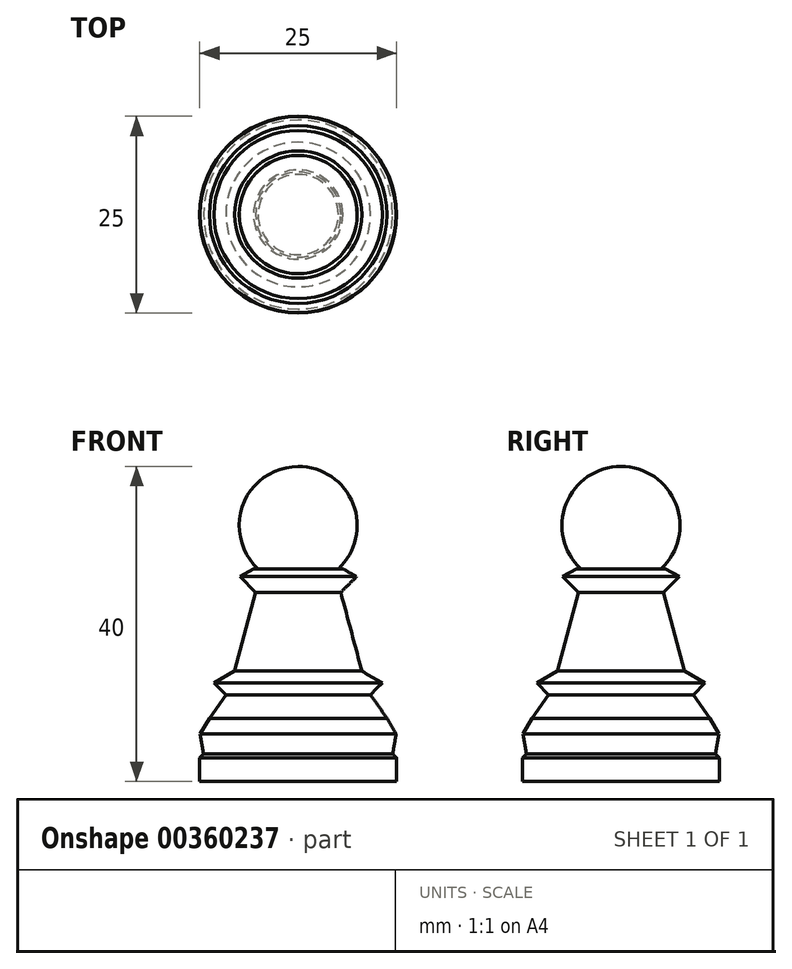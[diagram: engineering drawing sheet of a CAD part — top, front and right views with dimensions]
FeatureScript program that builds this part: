
annotation { "Feature Type Name" : "Feature", "Feature Type Description" : "" }
export const myFeature = defineFeature(function(context is Context, id is Id, definition is map)
    precondition{}
    {
        {
            var Q0;
            Q0=qCreatedBy(makeId("Top.planeOp"),FACE);
            var sketch = newSketch(context, id + "F0", { "sketchPlane" : qUnion([Q0])});
            skCircle(sketch, "E0", {"center": v(0, 0) * mm, "radius": 12.5 * mm});
            skSolve(sketch);
        }
        {
            var Q0;
            Q0=makeQuery(id+"F0.imprint","IMPRINT",FACE,{"disambiguationData":[TD([[makeQuery(id+"F0.imprint","IMPRINT",EDGE,{"derivedFrom":sQuery(id+"F0.wireOp",EDGE,"E0")}),1.0]])]});
            extrude(context, id + "F1", {"entities" : qUnion([Q0]), "depth" : 3 * mm});
        }
        {
            var Q0;
            Q0=makeQuery(id+"F1.opExtrude","CAP_FACE",FACE,{"disambiguationData":[OSD([sQuery(id+"F0.wireOp",EDGE,"E0")])],"isStart":false});
            extrude(context, id + "F2", {"entities" : qUnion([Q0]), "operationType" : NewBodyOperationType.ADD, "depth" : .5 * mm, "hasDraft" : true, "draftAngle" : 45 * degree, "draftPullDirection" : true});
        }
        {
            var Q0;
            Q0=makeQuery(id+"F2.opExtrude","CAP_FACE",FACE,{"disambiguationData":[OSD([sQuery(id+"F0.wireOp",EDGE,"E0")])],"isStart":false});
            extrude(context, id + "F3", {"entities" : qUnion([Q0]), "operationType" : NewBodyOperationType.ADD, "depth" : 2.5 * mm, "hasDraft" : true, "draftAngle" : 10 * degree});
        }
        {
            var Q0;
            Q0=makeQuery(id+"F3.opExtrude","CAP_FACE",FACE,{"disambiguationData":[OSD([sQuery(id+"F0.wireOp",EDGE,"E0")])],"isStart":false});
            extrude(context, id + "F4", {"entities" : qUnion([Q0]), "operationType" : NewBodyOperationType.ADD, "depth" : 2 * mm, "hasDraft" : true, "draftAngle" : 30 * degree, "draftPullDirection" : true});
        }
        {
            var Q0;
            Q0=makeQuery(id+"F4.opExtrude","CAP_FACE",FACE,{"disambiguationData":[OSD([sQuery(id+"F0.wireOp",EDGE,"E0")])],"isStart":false});
            extrude(context, id + "F5", {"entities" : qUnion([Q0]), "operationType" : NewBodyOperationType.ADD, "depth" : 3 * mm, "hasDraft" : true, "draftAngle" : 35 * degree, "draftPullDirection" : true});
        }
        {
            var Q0;
            Q0=makeQuery(id+"F5.opExtrude","CAP_FACE",FACE,{"disambiguationData":[OSD([sQuery(id+"F0.wireOp",EDGE,"E0")])],"isStart":false});
            extrude(context, id + "F6", {"entities" : qUnion([Q0]), "operationType" : NewBodyOperationType.ADD, "depth" : 1.5 * mm, "hasDraft" : true, "draftAngle" : 45 * degree});
        }
        {
            var Q0;
            Q0=makeQuery(id+"F6.opExtrude","CAP_FACE",FACE,{"disambiguationData":[OSD([sQuery(id+"F0.wireOp",EDGE,"E0")])],"isStart":false});
            extrude(context, id + "F7", {"entities" : qUnion([Q0]), "operationType" : NewBodyOperationType.ADD, "depth" : 1.5 * mm, "hasDraft" : true, "draftAngle" : 60 * degree, "draftPullDirection" : true});
        }
        {
            var Q0;
            Q0=makeQuery(id+"F7.opExtrude","CAP_FACE",FACE,{"disambiguationData":[OSD([sQuery(id+"F0.wireOp",EDGE,"E0")])],"isStart":false});
            extrude(context, id + "F8", {"entities" : qUnion([Q0]), "operationType" : NewBodyOperationType.ADD, "depth" : 10 * mm, "hasDraft" : true, "draftAngle" : 15 * degree, "draftPullDirection" : true});
        }
        {
            var Q0;
            Q0=makeQuery(id+"F8.opExtrude","CAP_FACE",FACE,{"disambiguationData":[OSD([sQuery(id+"F0.wireOp",EDGE,"E0")])],"isStart":false});
            extrude(context, id + "F9", {"entities" : qUnion([Q0]), "operationType" : NewBodyOperationType.ADD, "depth" : 2 * mm, "hasDraft" : true, "draftAngle" : 45 * degree});
        }
        {
            var Q0;
            Q0=makeQuery(id+"F9.opExtrude","CAP_FACE",FACE,{"disambiguationData":[OSD([sQuery(id+"F0.wireOp",EDGE,"E0")])],"isStart":false});
            extrude(context, id + "F10", {"entities" : qUnion([Q0]), "operationType" : NewBodyOperationType.ADD, "depth" : 1 * mm, "hasDraft" : true, "draftAngle" : 60 * degree, "draftPullDirection" : true});
        }
        {
            var Q0;
            Q0=qCreatedBy(makeId("Front.planeOp"),FACE);
            var sketch = newSketch(context, id + "F11", { "sketchPlane" : qUnion([Q0])});
            skLineSegment(sketch, "E1", {"start": v(0, 0) * mm, "end": v(0, 32.5) * mm});
            skCircle(sketch, "E2", {"center": v(0, 32.5) * mm, "radius": 7.5 * mm});
            skLineSegment(sketch, "E3", {"start": v(0, 32.5) * mm, "end": v(0, 55.1) * mm});
            skSolve(sketch);
        }
        {
            var Q0;
            {var subQ0=sQuery(id+"F11.wireOp",EDGE,"E3");var subQ1=sQuery(id+"F11.wireOp",EDGE,"E1");var subQ2=makeQuery(id+"F11.imprint","INTERSECT",VERTEX,{"derivedFrom":[subQ1,subQ0]});Q0=makeQuery(id+"F11.imprint","IMPRINT",FACE,{"disambiguationData":[TD([[makeQuery(id+"F11.imprint","IMPRINT",EDGE,{"disambiguationData":[TD([[subQ2,1.0]])],"derivedFrom":subQ1}),-1.0]])]});}
            var Q1;
            Q1=sQuery(id+"F11.wireOp",EDGE,"E3");
            revolve(context, id + "F12", {"operationType" : NewBodyOperationType.ADD, "entities" : qUnion([Q0]), "axis" : qUnion([Q1]), "revolveType" : RevolveType.FULL});
        }
    });
